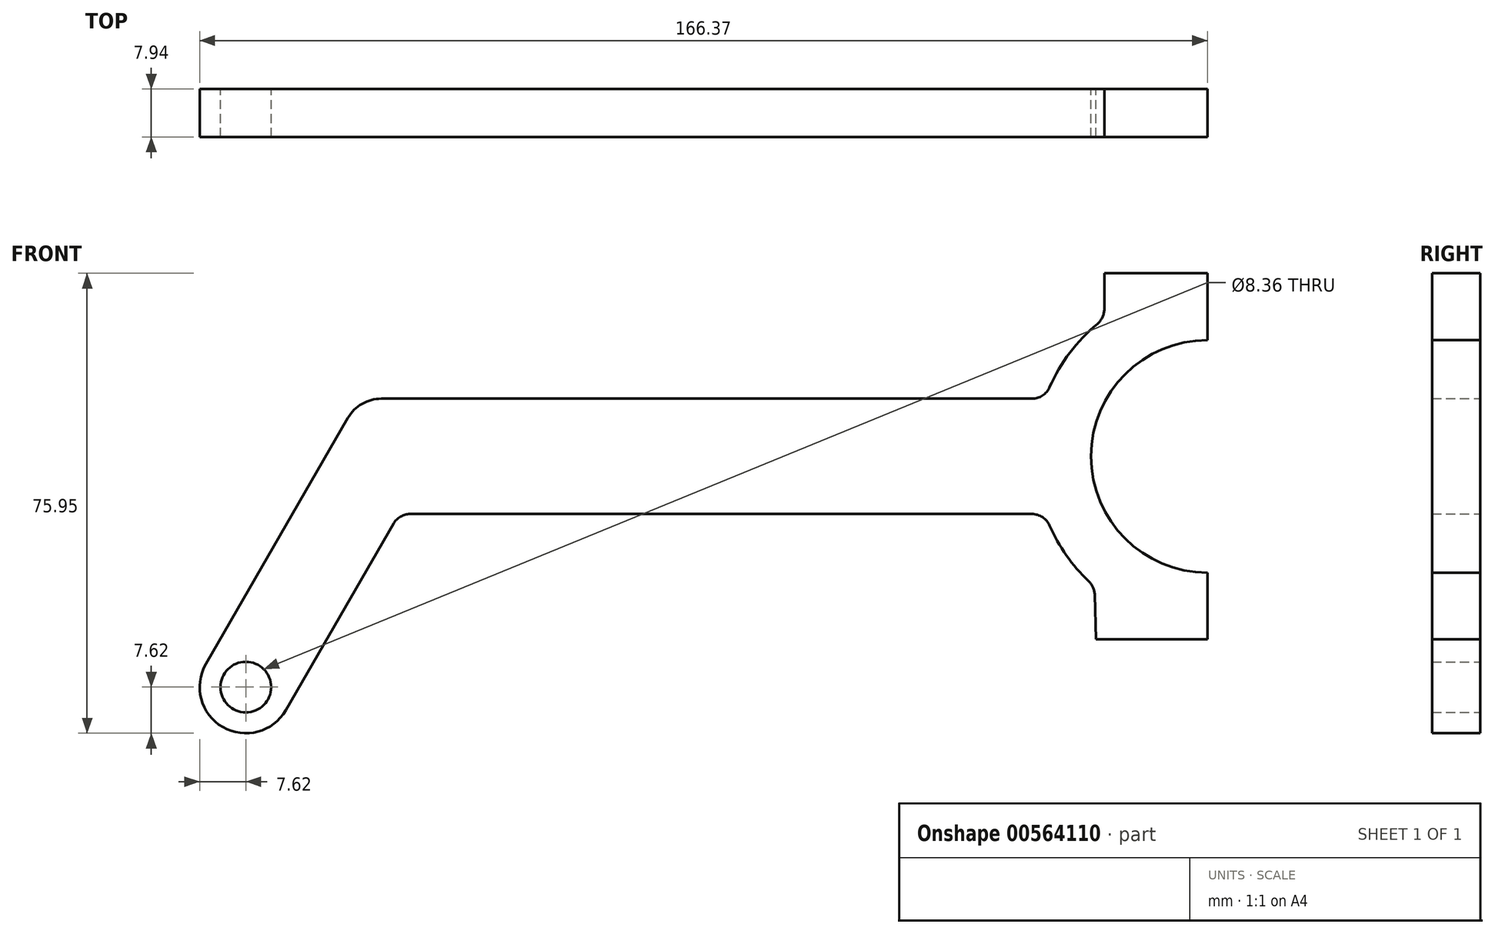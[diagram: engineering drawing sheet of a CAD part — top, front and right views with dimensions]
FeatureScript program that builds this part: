
annotation { "Feature Type Name" : "Feature", "Feature Type Description" : "" }
export const myFeature = defineFeature(function(context is Context, id is Id, definition is map)
    precondition{}
    {
        {
            var Q0;
            Q0=qCreatedBy(makeId("Front.planeOp"),FACE);
            var sketch = newSketch(context, id + "F0", { "sketchPlane" : qUnion([Q0])});
            skArc(sketch, "E0", {"start": v(0, 19.2) * mm, "mid": v(-19.2, 0) * mm, "end": v(0, -19.2) * mm});
            skCircle(sketch, "E1", {"center": v(-158.75, -38.1) * mm, "radius": 4.18 * mm});
            skArc(sketch, "E2", {"start": v(-18.17, 21.89) * mm, "mid": v(-22.72, 17.12) * mm, "end": v(-26.05, 11.42) * mm});
            skLineSegment(sketch, "E3", {"start": v(0, 30.23) * mm, "end": v(-17.02, 30.23) * mm});
            skLineSegment(sketch, "E4", {"start": v(-17.02, 30.23) * mm, "end": v(-17.02, 24.33) * mm});
            skLineSegment(sketch, "E5", {"start": v(0, -30.23) * mm, "end": v(-18.42, -30.23) * mm});
            skLineSegment(sketch, "E6", {"start": v(0, 30.23) * mm, "end": v(0, 19.2) * mm});
            skLineSegment(sketch, "E7", {"start": v(0, -19.2) * mm, "end": v(0, -30.23) * mm});
            skLineSegment(sketch, "E8", {"start": v(-28.96, 9.53) * mm, "end": v(-136.39, 9.52) * mm});
            skPoint(sketch, "E9.newPointA", {"position": v(-14.16, 24.68) * mm});
            skArc(sketch, "E10", {"start": v(-26.05, -11.42) * mm, "mid": v(-23.28, -16.34) * mm, "end": v(-19.6, -20.62) * mm});
            skLineSegment(sketch, "E11", {"start": v(-18.42, -30.23) * mm, "end": v(-18.61, -22.84) * mm});
            skPoint(sketch, "E12.newPointA", {"position": v(-17.02, 21.98) * mm});
            skPoint(sketch, "E12.newPointB", {"position": v(-18.06, 21.98) * mm});
            skArc(sketch, "E12.filletArc", {"start": v(-18.17, 21.89) * mm, "mid": v(-17.32, 22.98) * mm, "end": v(-17.02, 24.33) * mm});
            skPoint(sketch, "E13.visualSharp", {"position": v(-26.8, 9.53) * mm});
            skArc(sketch, "E13.filletArc", {"start": v(-28.96, 9.53) * mm, "mid": v(-27.22, 10.04) * mm, "end": v(-26.05, 11.42) * mm});
            skLineSegment(sketch, "E14", {"start": v(-28.96, -9.52) * mm, "end": v(-131.63, -9.53) * mm});
            skArc(sketch, "E15", {"start": v(-165.35, -34.3) * mm, "mid": v(-162.56, -44.7) * mm, "end": v(-152.15, -41.91) * mm});
            skLineSegment(sketch, "E16", {"start": v(-165.35, -34.3) * mm, "end": v(-141.89, 6.35) * mm});
            skLineSegment(sketch, "E17", {"start": v(-152.15, -41.91) * mm, "end": v(-134.38, -11.11) * mm});
            skArc(sketch, "E18.filletArc", {"start": v(-136.39, 9.52) * mm, "mid": v(-139.56, 8.67) * mm, "end": v(-141.89, 6.35) * mm});
            skPoint(sketch, "E19.visualSharp", {"position": v(-133.46, -9.53) * mm});
            skArc(sketch, "E19.filletArc", {"start": v(-131.63, -9.53) * mm, "mid": v(-133.22, -9.95) * mm, "end": v(-134.38, -11.11) * mm});
            skPoint(sketch, "E20.visualSharp", {"position": v(-26.8, -9.52) * mm});
            skArc(sketch, "E20.filletArc", {"start": v(-26.05, -11.42) * mm, "mid": v(-27.22, -10.04) * mm, "end": v(-28.96, -9.52) * mm});
            skPoint(sketch, "E21.newPointA", {"position": v(-18.6, -21.53) * mm});
            skPoint(sketch, "E21.newPointB", {"position": v(-18.65, -21.53) * mm});
            skArc(sketch, "E21.filletArc", {"start": v(-18.61, -22.84) * mm, "mid": v(-18.88, -21.63) * mm, "end": v(-19.6, -20.62) * mm});
            skSolve(sketch);
        }
        {
            var Q0;
            Q0=makeQuery(id+"F0.imprint","IMPRINT",FACE,{"disambiguationData":[TD([[makeQuery(id+"F0.imprint","IMPRINT",EDGE,{"derivedFrom":sQuery(id+"F0.wireOp",EDGE,"E0")}),-1.0]])]});
            extrude(context, id + "F1", {"entities" : qUnion([Q0]), "endBound" : BoundingType.SYMMETRIC, "depth" : 7.94 * mm, "offsetDistance" : 25.4 * mm});
        }
    });
